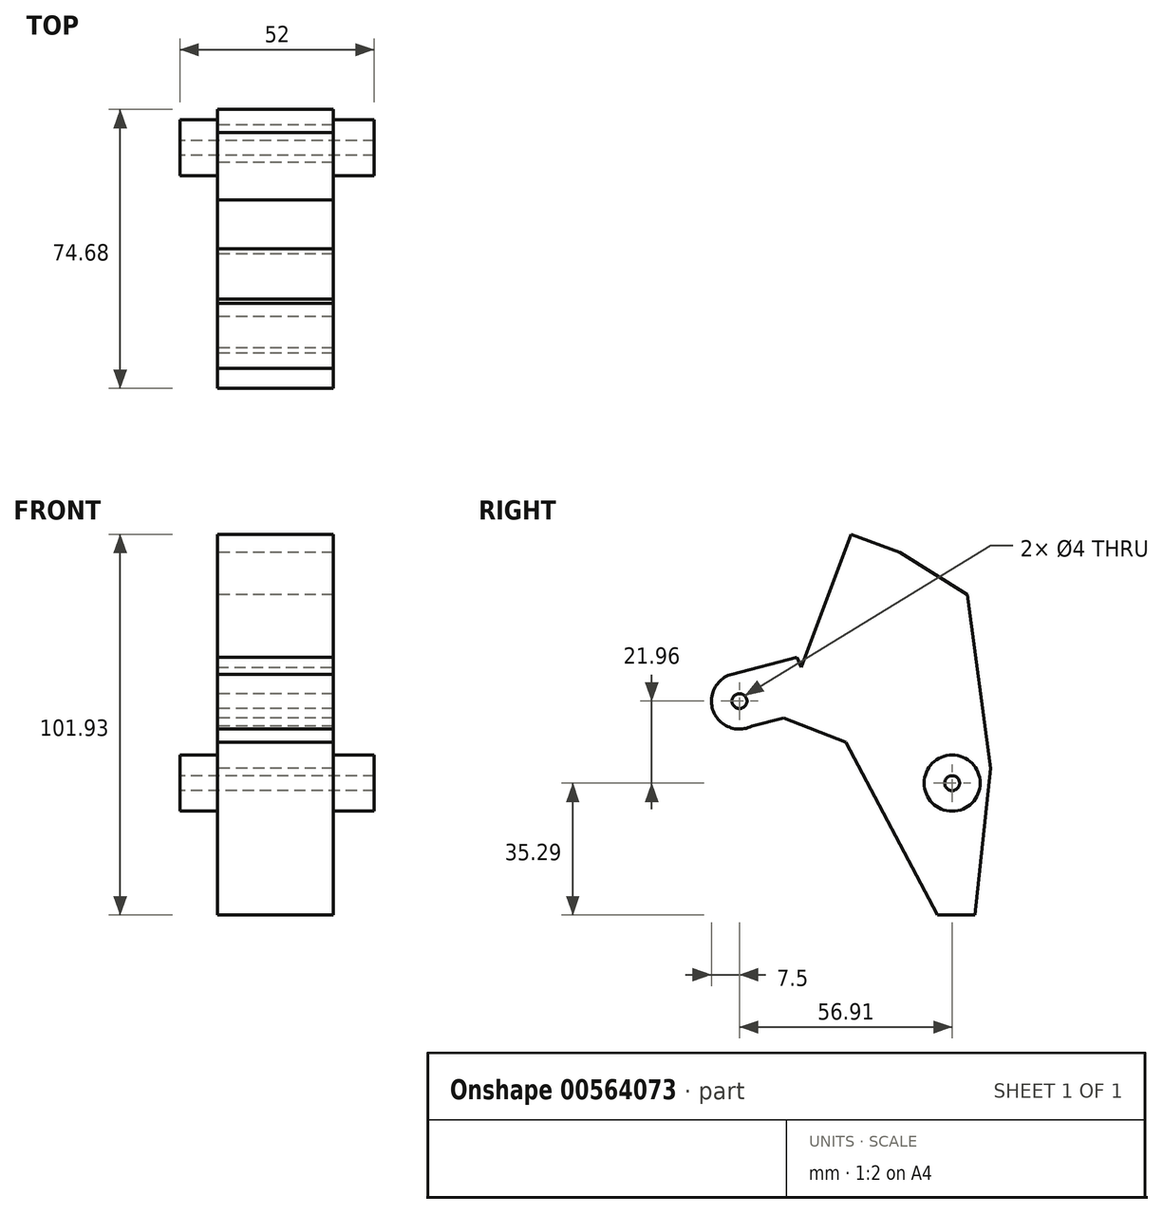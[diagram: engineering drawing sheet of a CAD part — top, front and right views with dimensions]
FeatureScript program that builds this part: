
annotation { "Feature Type Name" : "Feature", "Feature Type Description" : "" }
export const myFeature = defineFeature(function(context is Context, id is Id, definition is map)
    precondition{}
    {
        {
            var Q0;
            Q0=qCreatedBy(makeId("Right.planeOp"),FACE);
            var sketch = newSketch(context, id + "F0", { "sketchPlane" : qUnion([Q0])});
            skArc(sketch, "E0", {"start": v(40.97, 45.19) * mm, "mid": v(56.91, -21.96) * mm, "end": v(0, -61) * mm, "construction": true});
            skLineSegment(sketch, "E1", {"start": v(0, 0) * mm, "end": v(56.91, -21.96) * mm});
            skCircle(sketch, "E2", {"center": v(0, 0) * mm, "radius": 2 * mm});
            skCircle(sketch, "E3", {"center": v(56.91, -21.96) * mm, "radius": 2 * mm});
            skLineSegment(sketch, "E4", {"start": v(15.35, 11.68) * mm, "end": v(-2.08, 7.2) * mm});
            skLineSegment(sketch, "E5", {"start": v(11.8, -4.55) * mm, "end": v(3.32, -6.73) * mm});
            skArc(sketch, "E6", {"start": v(-2.08, 7.2) * mm, "mid": v(-7, -2.71) * mm, "end": v(3.32, -6.73) * mm});
            skCircle(sketch, "E7", {"center": v(56.91, -21.96) * mm, "radius": 7.5 * mm});
            skLineSegment(sketch, "E8", {"start": v(15.35, 11.68) * mm, "end": v(28.02, 45.38) * mm});
            skLineSegment(sketch, "E9", {"start": v(25.04, 37.47) * mm, "end": v(53, -57.25) * mm, "construction": true});
            skLineSegment(sketch, "E10", {"start": v(28.02, 45.38) * mm, "end": v(43, 39.75) * mm});
            skLineSegment(sketch, "E11", {"start": v(43, 39.75) * mm, "end": v(24.5, -9.45) * mm});
            skLineSegment(sketch, "E12", {"start": v(24.5, -9.45) * mm, "end": v(15.35, 11.68) * mm, "construction": true});
            skLineSegment(sketch, "E13", {"start": v(67.18, -18.02) * mm, "end": v(63, -57.25) * mm});
            skLineSegment(sketch, "E14", {"start": v(63, -57.25) * mm, "end": v(53, -57.25) * mm});
            skLineSegment(sketch, "E15", {"start": v(29.89, 44.68) * mm, "end": v(16.5, 9.04) * mm, "construction": true});
            skLineSegment(sketch, "E16", {"start": v(21.68, 28.53) * mm, "end": v(-18.42, 43.6) * mm, "construction": true});
            skLineSegment(sketch, "E17", {"start": v(0, 0) * mm, "end": v(0, -59.92) * mm, "construction": true});
            skLineSegment(sketch, "E18", {"start": v(0, -59.92) * mm, "end": v(58, -59.92) * mm, "construction": true});
            skLineSegment(sketch, "E19", {"start": v(0, 0) * mm, "end": v(-18.15, -62.41) * mm, "construction": true});
            skLineSegment(sketch, "E20", {"start": v(-18.15, -62.41) * mm, "end": v(40.11, -83.62) * mm, "construction": true});
            skLineSegment(sketch, "E21", {"start": v(63.2, -85) * mm, "end": v(18.2, -85) * mm, "construction": true});
            skLineSegment(sketch, "E22", {"start": v(43, 39.75) * mm, "end": v(61.02, 28.53) * mm});
            skLineSegment(sketch, "E23", {"start": v(61.02, 28.53) * mm, "end": v(67.18, -18.02) * mm});
            skLineSegment(sketch, "E24", {"start": v(53, -57.25) * mm, "end": v(28.46, -10.98) * mm});
            skLineSegment(sketch, "E25", {"start": v(18.19, 13.54) * mm, "end": v(18.19, -7.02) * mm});
            skSolve(sketch);
        }
        {
            var Q0;
            Q0=qCreatedBy(makeId("Front.planeOp"),FACE);
            var sketch = newSketch(context, id + "F1", { "sketchPlane" : qUnion([Q0])});
            skLineSegment(sketch, "E26", {"start": v(-45.02, 46.54) * mm, "end": v(49.25, 46.54) * mm, "construction": true});
            skPoint(sketch, "E27.0", {"position": v(0, 28.53) * mm});
            skPoint(sketch, "E28.0", {"position": v(0, 36.07) * mm});
            skLineSegment(sketch, "E29.0", {"start": v(0, 28.53) * mm, "end": v(0, 43.6) * mm, "construction": true});
            skSolve(sketch);
        }
        {
            var Q0;
            Q0=qCreatedBy(makeId("Front.planeOp"),FACE);
            var Q1;
            Q1=sQuery(id+"F1.wireOp",EDGE,"E26");
            cPlane(context, id + "F2", {"entities" : qUnion([Q0, Q1]), "cplaneType" : CPlaneType.LINE_ANGLE, "offset" : 25 * mm, "angle" : 50 * degree, "oppositeDirection" : true, "width" : 150 * mm, "height" : 150 * mm});
        }
        {
            var Q0;
            {var subQ4=sQuery(id+"F0.wireOp",EDGE,"bTAcjFBJ-pDFs-YPlj-GWIW-IK2A0WvhptIx");Q0=makeQuery(id+"F0.imprint","IMPRINT",FACE,{"disambiguationData":[TD([[makeQuery(id+"F0.imprint","IMPRINT",EDGE,{"derivedFrom":subQ4}),1.0]])]});}
            var Q1;
            {var subQ0=sQuery(id+"F0.wireOp",EDGE,"E11");Q1=makeQuery(id+"F0.imprint","IMPRINT",FACE,{"disambiguationData":[TD([[makeQuery(id+"F0.imprint","IMPRINT",EDGE,{"derivedFrom":subQ0}),1.0]])]});}
            var Q2;
            {var subQ0=sQuery(id+"F0.wireOp",EDGE,"E14");Q2=makeQuery(id+"F0.imprint","IMPRINT",FACE,{"disambiguationData":[TD([[makeQuery(id+"F0.imprint","IMPRINT",EDGE,{"derivedFrom":subQ0}),-1.0]])]});}
            var Q3;
            Q3=makeQuery(id+"F0.imprint","IMPRINT",FACE,{"disambiguationData":[TD([[makeQuery(id+"F0.imprint","IMPRINT",EDGE,{"derivedFrom":sQuery(id+"F0.wireOp",EDGE,"E2")}),-1.0]])]});
            extrude(context, id + "F3", {"entities" : qUnion([Q0, Q1, Q2, Q3]), "depth" : 15 * mm, "offsetDistance" : 25 * mm, "hasSecondDirection" : true, "secondDirectionOppositeDirection" : true, "secondDirectionDepth" : 16 * mm});
        }
        {
            var Q0;
            Q0=makeQuery(id+"F0.imprint","IMPRINT",FACE,{"disambiguationData":[TD([[makeQuery(id+"F0.imprint","IMPRINT",EDGE,{"derivedFrom":sQuery(id+"F0.wireOp",EDGE,"E3")}),-1.0]])]});
            extrude(context, id + "F4", {"entities" : qUnion([Q0]), "operationType" : NewBodyOperationType.ADD, "depth" : 26 * mm, "offsetDistance" : 25 * mm, "hasSecondDirection" : true, "secondDirectionOppositeDirection" : true, "secondDirectionDepth" : 26 * mm});
        }
        {
            var Q0;
            Q0=qCreatedBy(makeId("Right.planeOp"),FACE);
            var sketch = newSketch(context, id + "F5", { "sketchPlane" : qUnion([Q0])});
            skLineSegment(sketch, "E30.0", {"start": v(29.89, 44.68) * mm, "end": v(16.5, 9.04) * mm});
            skLineSegment(sketch, "E31.0", {"start": v(15.35, 11.68) * mm, "end": v(28.02, 45.38) * mm});
            skLineSegment(sketch, "E32.0", {"start": v(24.5, -9.45) * mm, "end": v(15.35, 11.68) * mm});
            skLineSegment(sketch, "E33.0", {"start": v(28.02, 45.38) * mm, "end": v(43, 39.75) * mm});
            skSolve(sketch);
        }
        {
            var Q0;
            {var subQ0=sQuery(id+"F5.wireOp",EDGE,"E30.0");Q0=makeQuery(id+"F5.imprint","IMPRINT",FACE,{"disambiguationData":[TD([[makeQuery(id+"F5.imprint","IMPRINT",EDGE,{"derivedFrom":subQ0}),-1.0]])]});}
            extrude(context, id + "F6", {"entities" : qUnion([Q0]), "operationType" : NewBodyOperationType.REMOVE, "oppositeDirection" : true, "depth" : 25 * mm, "offsetDistance" : 25 * mm, "hasSecondDirection" : true, "secondDirectionOppositeDirection" : false, "secondDirectionDepth" : 25 * mm});
        }
    });
